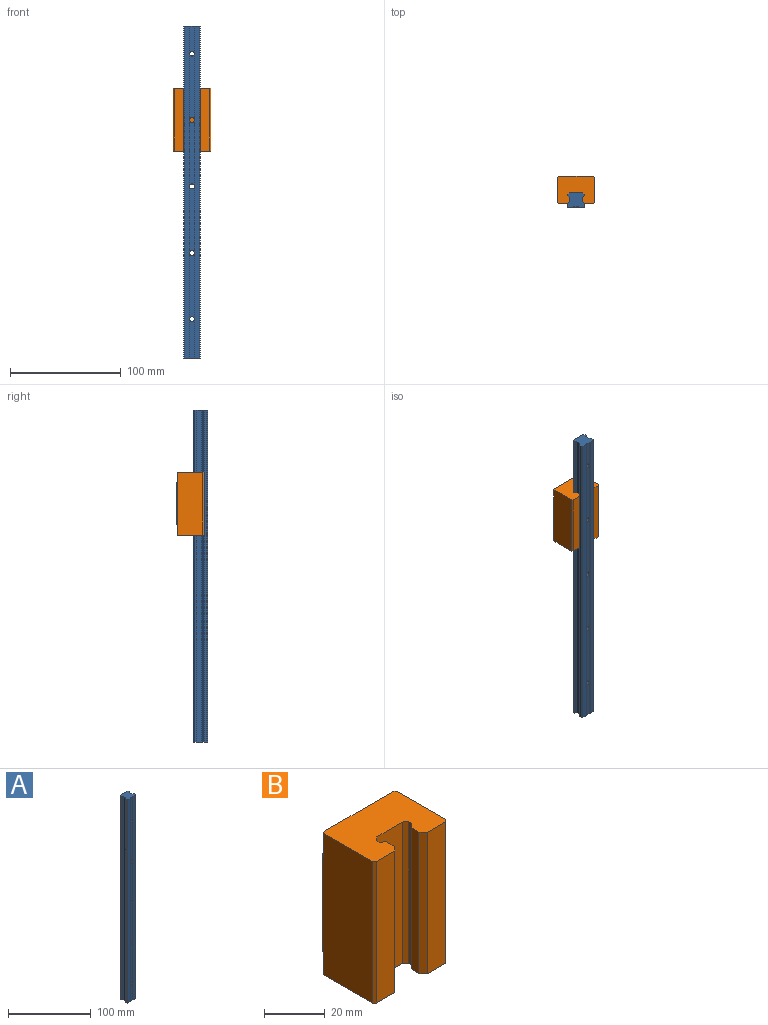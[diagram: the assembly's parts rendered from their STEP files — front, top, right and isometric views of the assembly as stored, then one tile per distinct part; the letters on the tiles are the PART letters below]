
ASSEMBLY  parts=2 mates=2
PART A: 42 faces, bbox 15x13x300 mm
  f0: plane 23.67x3.63mm, normal (0,-1,0), area 83.5mm2, adj f15,f17,f26,f39
  f1: plane 57.34x3.63mm, normal (0,-1,0), area 203.3mm2, adj f15,f17,f36,f39
  f2: plane 57.34x3.63mm, normal (0,-1,0), area 203.3mm2, adj f15,f17,f33,f36
  f3: plane 57.34x3.63mm, normal (0,-1,0), area 203.3mm2, adj f15,f17,f30,f33
  f4: plane 57.34x3.63mm, normal (0,-1,0), area 203.3mm2, adj f15,f17,f27,f30
  f5: plane 300x1.51mm, normal (0.68,0.73,0), area 618.1mm2, adj f6,f24,f25,f26
  f6: plane 300x11.97mm, normal (0,1,0), area 3371mm2, adj f5,f7,f25,f26,f29,f32,f35,f38
  f7: plane 300x1.51mm, normal (-0.68,0.73,0), area 618.1mm2, adj f6,f8,f25,f26
  f8: plane 300x1.27mm, normal (-1,0,0), area 381.4mm2, adj f7,f9,f25,f26
  f9: plane 300x1.76mm, normal (-0.66,-0.75,0), area 703.6mm2, adj f8,f10,f25,f26
  f10: plane 300x3.62mm, normal (-1,0,0), area 1086.6mm2, adj f9,f11,f25,f26
  f11: plane 300x2.02mm, normal (-0.75,0.66,0), area 803.6mm2, adj f10,f12,f25,f26
  f12: plane 300x2.46mm, normal (-1,0,0), area 737.8mm2, adj f11,f13,f25,f26
  f13: plane 300x0.68mm, normal (-0.71,-0.71,0), area 290.4mm2, adj f12,f14,f25,f26
  f14: plane 300x4.56mm, normal (0,-1,0), area 1367.9mm2, adj f13,f15,f25,f26
  f15: plane 300x0.52mm, normal (0.76,-0.65,0), area 198.4mm2, adj f0,f1,f2,f3,f4,f14,f16,f25
  f16: plane 33.67x3.63mm, normal (0,-1,0), area 119.8mm2, adj f15,f17,f25,f27
  f17: plane 300x0.52mm, normal (-0.76,-0.65,0), area 198.4mm2, adj f0,f1,f2,f3,f4,f16,f18,f25
  f18: plane 300x4.56mm, normal (0,-1,0), area 1367.9mm2, adj f17,f19,f25,f26
  f19: plane 300x0.68mm, normal (0.71,-0.71,0), area 290.4mm2, adj f18,f20,f25,f26
  f20: plane 300x2.46mm, normal (1,0,0), area 737.8mm2, adj f19,f21,f25,f26
  f21: plane 300x2.02mm, normal (0.75,0.66,0), area 803.6mm2, adj f20,f22,f25,f26
  f22: plane 300x3.62mm, normal (1,0,0), area 1086.6mm2, adj f21,f23,f25,f26
  f23: plane 300x1.76mm, normal (0.66,-0.75,0), area 703.6mm2, adj f22,f24,f25,f26
  f24: plane 300x1.27mm, normal (1,0,0), area 381.4mm2, adj f5,f23,f25,f26
  f25: plane 15x13mm, normal (0,0,1), area 171.3mm2, adj f5,f6,f7,f8,f9,f10,f11,f12
  f26: plane 15x13mm, normal (0,0,-1), area 171.3mm2, adj f0,f5,f6,f7,f8,f9,f10,f11
  f27: cylinder r=2.25mm len=7.49mm, axis (0,1,0), area 100.6mm2, adj f4,f15,f16,f17,f28
  f28: plane 7.5x7.5mm, normal (0,1,0), area 28.3mm2, adj f27,f29
  f29: cylinder r=3.75mm len=7.5mm, axis (0,1,0), area 129.6mm2, adj f6,f28
  f30: cylinder r=2.25mm len=7.49mm, axis (0,1,0), area 100.6mm2, adj f3,f4,f15,f17,f31
  f31: plane 7.5x7.5mm, normal (0,1,0), area 28.3mm2, adj f30,f32
  f32: cylinder r=3.75mm len=7.5mm, axis (0,1,0), area 129.6mm2, adj f6,f31
  f33: cylinder r=2.25mm len=7.49mm, axis (0,1,0), area 100.6mm2, adj f2,f3,f15,f17,f34
  f34: plane 7.5x7.5mm, normal (0,1,0), area 28.3mm2, adj f33,f35
  f35: cylinder r=3.75mm len=7.5mm, axis (0,1,0), area 129.6mm2, adj f6,f34
  f36: cylinder r=2.25mm len=7.49mm, axis (0,1,0), area 100.6mm2, adj f1,f2,f15,f17,f37
  f37: plane 7.5x7.5mm, normal (0,1,0), area 28.3mm2, adj f36,f38
  f38: cylinder r=3.75mm len=7.5mm, axis (0,1,0), area 129.6mm2, adj f6,f37
  f39: cylinder r=2.25mm len=7.49mm, axis (0,1,0), area 100.6mm2, adj f0,f1,f15,f17,f40
  f40: plane 7.5x7.5mm, normal (0,1,0), area 28.3mm2, adj f39,f41
  f41: cylinder r=3.75mm len=7.5mm, axis (0,1,0), area 129.6mm2, adj f6,f40
PART B: 47 faces, bbox 34x25x56.8 mm
  f0: plane 38.2x7.37mm, normal (0,1,0), area 252.6mm2, adj f3,f24,f30,f36,f37,f38
  f1: plane 34x24.3mm, normal (0,0,-1), area 697.9mm2, adj f4,f5,f6,f7,f9,f10,f11,f12
  f2: plane 38.2x1mm, normal (-0.71,0.71,0), area 54mm2, adj f8,f9,f35,f39
  f3: plane 38.2x1mm, normal (0.71,0.71,0), area 54mm2, adj f0,f7,f36,f38
  f4: plane 56.8x3.62mm, normal (-1,0,0), area 205.7mm2, adj f1,f5,f19,f20
  f5: plane 56.8x2.01mm, normal (-0.75,-0.66,0), area 151.6mm2, adj f1,f4,f6,f20
  f6: plane 56.8x8.51mm, normal (0,-1,0), area 483.2mm2, adj f1,f5,f20,f22
  f7: plane 56.8x23mm, normal (1,0,0), area 1302mm2, adj f1,f3,f20,f22,f36,f38,f45,f46
  f8: plane 38.2x7.37mm, normal (0,1,0), area 252.6mm2, adj f2,f26,f28,f34,f35,f39
  f9: plane 56.8x23mm, normal (-1,0,0), area 1302mm2, adj f1,f2,f20,f21,f35,f39,f43,f44
  f10: plane 56.8x8.51mm, normal (0,-1,0), area 483.1mm2, adj f1,f11,f20,f21
  f11: plane 56.8x2.01mm, normal (0.75,-0.66,0), area 151.6mm2, adj f1,f10,f12,f20
  f12: plane 56.8x3.62mm, normal (1,0,0), area 205.7mm2, adj f1,f11,f13,f20
  f13: plane 56.8x1.76mm, normal (0.66,0.75,0), area 133.2mm2, adj f1,f12,f14,f20
  f14: plane 56.8x1.27mm, normal (1,0,0), area 72.2mm2, adj f1,f13,f15,f20
  f15: plane 56.8x1.51mm, normal (0.68,-0.73,0), area 117mm2, adj f1,f14,f16,f20
  f16: plane 56.8x11.97mm, normal (0,-1,0), area 680.1mm2, adj f1,f15,f17,f20
  f17: plane 56.8x1.51mm, normal (-0.68,-0.73,0), area 117mm2, adj f1,f16,f18,f20
  f18: plane 56.8x1.27mm, normal (-1,0,0), area 72.2mm2, adj f1,f17,f19,f20
  f19: plane 56.8x1.76mm, normal (-0.66,0.75,0), area 133.2mm2, adj f1,f4,f18,f20
  f20: plane 34x24.3mm, normal (0,0,1), area 697.9mm2, adj f4,f5,f6,f7,f9,f10,f11,f12
  f21: plane 56.8x1mm, normal (-0.71,-0.71,0), area 80.3mm2, adj f1,f9,f10,f20
  f22: plane 56.8x1mm, normal (0.71,-0.71,0), area 80.3mm2, adj f1,f6,f7,f20
  f23: cone r=0mm half-angle=59deg, axis (0,1,0), area 16.9mm2, adj f24
  f24: cylinder r=2.15mm len=5mm, axis (0,1,0), area 67.5mm2, adj f0,f23
  f25: cone r=0mm half-angle=59deg, axis (0,1,0), area 16.9mm2, adj f26
  f26: cylinder r=2.15mm len=5mm, axis (0,1,0), area 67.5mm2, adj f8,f25
  f27: cone r=0mm half-angle=59deg, axis (0,1,0), area 16.9mm2, adj f28
  f28: cylinder r=2.15mm len=5mm, axis (0,1,0), area 67.5mm2, adj f8,f27
  f29: cone r=0mm half-angle=59deg, axis (0,1,0), area 16.9mm2, adj f30
  f30: cylinder r=2.15mm len=5mm, axis (0,1,0), area 67.5mm2, adj f0,f29
  f31: plane 38.2x0.7mm, normal (1,0,0), area 26.7mm2, adj f32,f40,f41,f42
  f32: plane 7.36x0.7mm, normal (0,0,1), area 5.1mm2, adj f31,f33,f41,f42
  f33: plane 38.2x0.7mm, normal (-1,0,0), area 26.7mm2, adj f32,f40,f41,f42
  f34: plane 38.2x0.7mm, normal (1,0,0), area 26.7mm2, adj f8,f35,f39,f41
  f35: plane 8.37x1.24mm, normal (0,0,1), area 5.7mm2, adj f2,f8,f9,f34,f41,f43
  f36: plane 8.37x1.24mm, normal (0,0,1), area 5.7mm2, adj f0,f3,f7,f37,f41,f45
  f37: plane 38.2x0.7mm, normal (-1,0,0), area 26.7mm2, adj f0,f36,f38,f41
  f38: plane 8.37x1.24mm, normal (0,0,-1), area 5.7mm2, adj f0,f3,f7,f37,f41,f46
  f39: plane 8.37x1.24mm, normal (0,0,-1), area 5.7mm2, adj f2,f8,f9,f34,f41,f44
  f40: plane 7.36x0.7mm, normal (0,0,-1), area 5.1mm2, adj f31,f33,f41,f42
  f41: plane 56.8x31.4mm, normal (0,1,0), area 962.2mm2, adj f1,f20,f31,f32,f33,f34,f35,f36
  f42: plane 38.2x7.36mm, normal (0,1,0), area 281mm2, adj f31,f32,f33,f40
  f43: plane 9.3x1.3mm, normal (-0.38,0.92,0), area 13.1mm2, adj f9,f20,f35,f41
  f44: plane 9.3x1.3mm, normal (-0.38,0.92,0), area 13.1mm2, adj f1,f9,f39,f41
  f45: plane 9.3x1.3mm, normal (0.38,0.92,0), area 13.1mm2, adj f7,f20,f36,f41
  f46: plane 9.3x1.3mm, normal (0.38,0.92,0), area 13.1mm2, adj f1,f7,f38,f41
PLACE A rot(axis=(0,-1,0),180deg) t=(-99.33,-22.73,316.82)mm
PLACE B rot(axis=(0,1,0),180deg) t=(-99.33,-19.57,260.49)mm
MATE planar A.f33 <-> B.f16  axis (0,1,0) through (-99.33,-9.73,171.82)mm
MATE planar B.f4 <-> A.f22  axis (1,0,0) through (-105.07,-13.94,203.69)mm
